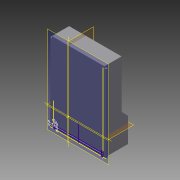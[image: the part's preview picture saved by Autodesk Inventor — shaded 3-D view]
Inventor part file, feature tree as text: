
AUTODESK INVENTOR PART (.ipt)
format: ipt  version: 2015 (Build 190159000, 159)  size: 210,432 bytes
history: native  units: mm
features: extrude x9, sketch x8, projected_geometry x4
ambient origin geometry x8: Origin, YZ Plane, XZ Plane, XY Plane, X Axis, Y Axis, Z Axis, Center Point
bodies: Solid1 (feature_tree)
feature tree (21):
  extrude  "Extrusion1"  Depth=96.5mm
  extrude  "Extrusion2"  TaperAngle=0.0deg  [1 undecoded]
  extrude  "Extrusion3"  Depth=2.0mm
  extrude  "Extrusion4"  Depth=2.0mm
  extrude  "Extrusion5"  Depth=2.0mm
  extrude  "Extrusion6"  Depth=2.0mm TaperAngle=0.0deg
  extrude  "Extrusion7"  Depth=2.0mm
  sketch  "Sketch14"  dims[d18=2.0mm d19=0.0mm d20=27.0mm d21=10.0mm d22=45.0deg d23=2.0mm d24=0.0mm d25=2.0mm d26=2.0mm d27=0.0mm d46=10.0mm d47=15.0mm d48=2.0mm d49=0.0mm d50=6.0mm d51=2.0mm d52=2.0mm d53=2.0mm d54=2.0mm d55=2.0mm d56=2.0mm d57=0.0mm d60=2.0mm d61=0.0mm]
  extrude  "Extrusion8"  Depth=27.0mm
  extrude  "Extrusion10"  Depth=10.0mm
  sketch  "Sketch1"  dims[d0=68.0mm d1=96.5mm]
  sketch  "Sketch3"  dims[d2=2.0mm d3=0.0mm d4=0.0mm]
  projected_geometry  "Projected Loop1"
  sketch  "Sketch4"  dims[d5=2.0mm d7=2.0mm]
  projected_geometry  "Projected Loop2"
  sketch  "Sketch5"  dims[d8=0.0mm d9=2.0mm]
  projected_geometry  "Projected Loop3"
  projected_geometry  "Projected Loop4"
  sketch  "Sketch6"  dims[d10=2.0mm d11=2.0mm]
  sketch  "Sketch7"  dims[d12=25.0mm d13=0.0mm d14=2.0mm d15=0.0mm]
  sketch  "Sketch13"  dims[d16=2.0mm d17=2.0mm]
note: 1 required parameter value undecoded (feature->parameter linkage not recoverable at this tier; creation-order binding heuristic only, values carry confidence <= 0.55)
